# Revit family: Faucet-Deck_Mount-Bath-KOHLER-PURIST-K-14428T
name_source: partatom
category: Plumbing Fixtures
revit_build: Autodesk Revit 2017 (Build: 20160225_1515(x64)
units: mm (PartAtom-declared; Revit-internal decimal feet)

## family parameters
Cut with Voids When Loaded = No
Host = Face
OmniClass Number = 23.31.11.00
OmniClass Title = Faucets
Part Type = Normal
Room Calculation Point = No
Round Connector Dimension = Use Diameter
Shared = No

## types (12) — shared parameters
ADA Compliant = No
Assembly Code = D2010
CW Connection = Yes
Cold Water Inlet = Cold Water Inlet
Date Modified = 08/20/2020
Default Elevation = 36"
Drain Included = Yes
Flow Rate = 0 GPM
HW Connection = Yes
Height = 11 3/8"
Hot Water Inlet = Hot Water Inlet
Length = 7 1/2"
Manufacturer = KOHLER Co.
Master Format 2014 = 22 41 39
Master Format 2014 Name = Residential Faucets, Supplies, and Trim
Material = Premium Metal Construction
Pressure = 0.00 psi
Product Name = Purist
Spout Reach = 7 1/2"
URL = http://www.kohler.com.cn
Vent Connection = No
Waste Connection = No
Waste Water Outlet = Waste Water Outlet
WaterSense Certified = No

## per-type parameters (varying)
| type | Cross Handle | Description | Dist | Finish | Handle Clearance | Lever Handle | Model | Product Documentation Link | Product Page URL | Type |
| Cross Handle, CP-Polished Chrome | Yes | bathtub faucet with cross handle | 1 3/4" | Kohler-Metal-CP-Polished_Chrome | 3 1/2" | No | K-14428T-3-CP | https://files.kohler.com.cn | https://www.kohler.com.cn | 1 |
| Lever Handle, CP-Polished Chrome | No | Deck mount bath faucet- lever handle | 0" | Kohler-Metal-CP-Polished_Chrome | 2 5/8" | Yes | K-14428T-4-CP |  |  | 7 |
| Cross Handle,RGD- Rose Gold | Yes | bathtub faucet with cross handle | 1 3/4" | Kohler-Metal-RGD-Rose_Gold | 3 1/2" | No | K-14428T-3-RGD | https://files.kohler.com.cn | https://www.kohler.com.cn | 3 |
| Lever Handle, PGD-Eternal Gold | No | Deck mount bath faucet- lever handle | 0" | Kohler-Metal-PGD-Eternal_Gold | 2 5/8" | Yes | K-14428T-4-PGD |  |  | 11 |
| Cross Handle,BN- Roman Gold | Yes | bathtub faucet with cross handle | 1 3/4" | Kohler-Metal-BN-Roman_Silver | 3 1/2" | No | K-14428T-3-BN | https://files.kohler.com.cn | https://www.kohler.com.cn | 2 |
| Cross Handle,BGD- Roman Gold | Yes | bathtub faucet with cross handle | 1 3/4" | Kohler-Metal-BGD-Romankin | 3 1/2" | No | K-14428T-3-BGD | https://files.kohler.com.cn | https://www.kohler.com.cn | 4 |
| Cross Handle,PGD- Eternal Gold | Yes | bathtub faucet with cross handle | 1 3/4" | Kohler-Metal-PGD-Eternal_Gold | 3 1/2" | No | K-14428T-3-PGD | https://files.kohler.com.cn | https://www.kohler.com.cn | 5 |
| Cross Handle,SN-Champange Gold | Yes | bathtub faucet with cross handle | 1 3/4" | Kohler-Metal-SN-Champagne_Gold | 3 1/2" | No | K-14428T-3-SN | https://files.kohler.com.cn | https://www.kohler.com.cn | 6 |
| Lever Handle, BN- Roman Gold | No | Deck mount bath faucet- lever handle | 0" | Kohler-Metal-BN-Roman_Silver | 2 5/8" | Yes | K-14428T-4-BN |  |  | 8 |
| Lever Handle, RGD- Rose Gold | No | Deck mount bath faucet- lever handle | 0" | Kohler-Metal-RGD-Rose_Gold | 2 5/8" | Yes | K-14428T-4-RGD |  |  | 9 |
| Lever Handle, BGD- Roman Gold | No | Deck mount bath faucet- lever handle | 0" | Kohler-Metal-BGD-Romankin | 2 5/8" | Yes | K-14428T-4-BGD |  |  | 10 |
| Lever Handle, SN- Champangel Gold | No | Deck mount bath faucet- lever handle | 0" | Kohler-Metal-SN-Champagne_Gold | 2 5/8" | Yes | K-14428T-4-SN |  |  | 12 |

## geometry (parser evidence)
native form markers: Sweep x9
no freeform markers — native parametric forms only
